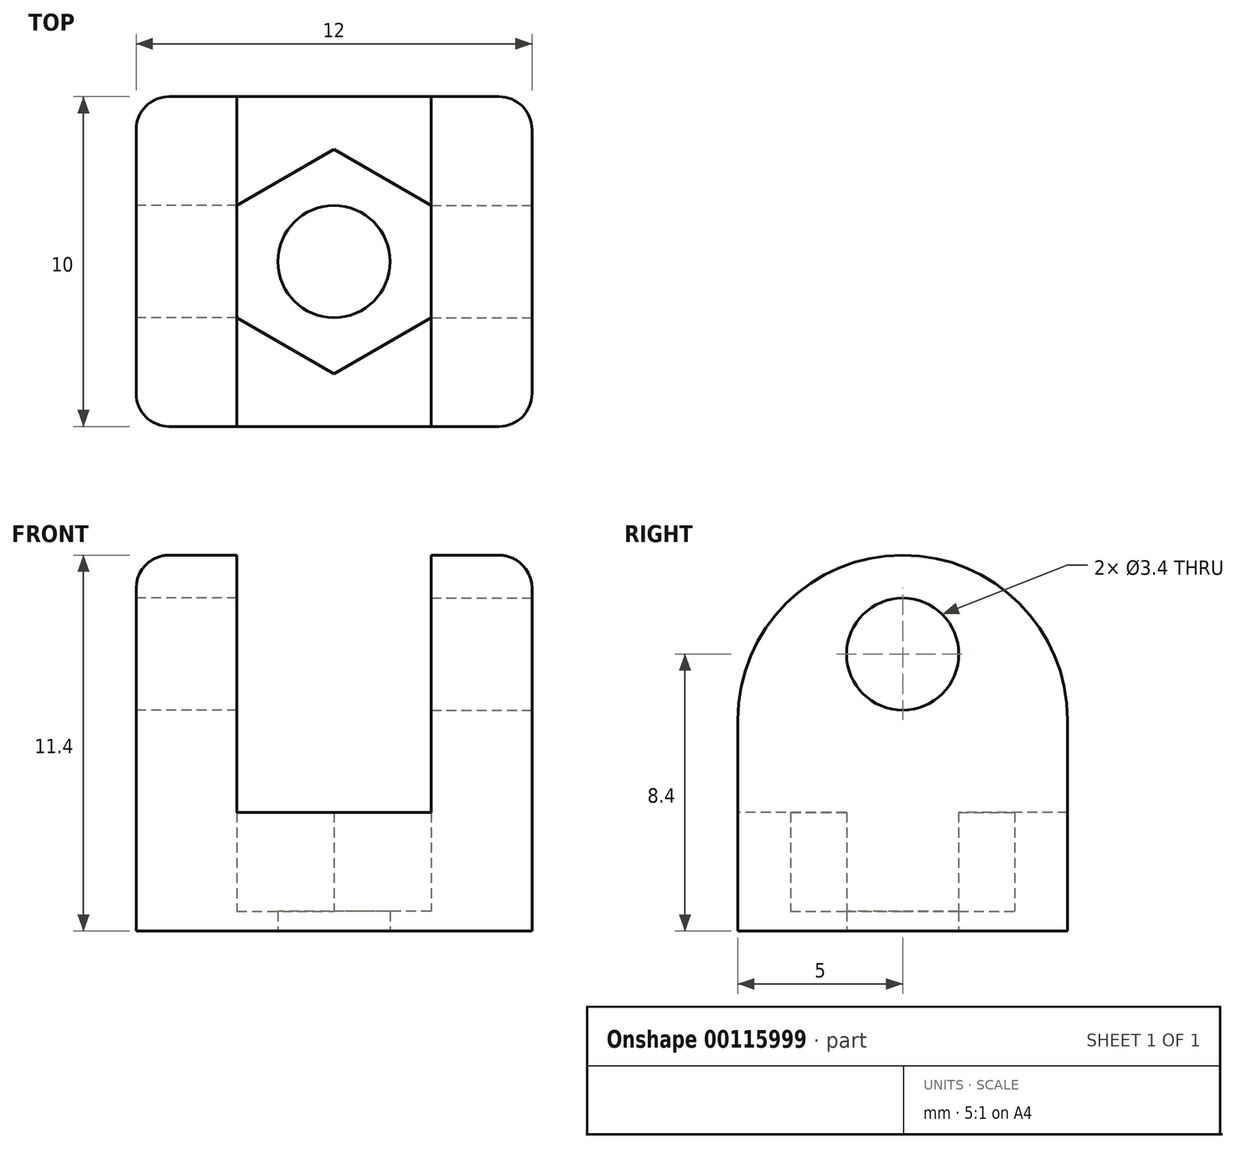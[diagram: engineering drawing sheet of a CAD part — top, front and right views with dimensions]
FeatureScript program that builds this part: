
annotation { "Feature Type Name" : "Feature", "Feature Type Description" : "" }
export const myFeature = defineFeature(function(context is Context, id is Id, definition is map)
    precondition{}
    {
        {
            var Q0;
            Q0=qCreatedBy(makeId("Top.planeOp"),FACE);
            var sketch = newSketch(context, id + "F0", { "sketchPlane" : qUnion([Q0])});
            skLineSegment(sketch, "E0.bottom", {"start": v(-6, 5) * mm, "end": v(6, 5) * mm});
            skLineSegment(sketch, "E0.top", {"start": v(-6, -5) * mm, "end": v(6, -5) * mm});
            skLineSegment(sketch, "E0.left", {"start": v(-6, 5) * mm, "end": v(-6, -5) * mm});
            skLineSegment(sketch, "E0.right", {"start": v(6, 5) * mm, "end": v(6, -5) * mm});
            skLineSegment(sketch, "E1", {"start": v(-2.94, 5) * mm, "end": v(-2.94, -5) * mm});
            skLineSegment(sketch, "E2", {"start": v(2.94, 5) * mm, "end": v(2.94, -5) * mm});
            skCircle(sketch, "E3", {"center": v(0, 0) * mm, "radius": 1.7 * mm});
            skCircle(sketch, "E4.cCircle", {"center": v(0, 0) * mm, "radius": 3.4 * mm, "construction": true});
            skLineSegment(sketch, "E4.0", {"start": v(0, 3.4) * mm, "end": v(2.94, 1.7) * mm});
            skLineSegment(sketch, "E4.1", {"start": v(2.94, 1.7) * mm, "end": v(2.94, -1.7) * mm});
            skLineSegment(sketch, "E4.2", {"start": v(2.94, -1.7) * mm, "end": v(0, -3.4) * mm});
            skLineSegment(sketch, "E4.3", {"start": v(0, -3.4) * mm, "end": v(-2.94, -1.7) * mm});
            skLineSegment(sketch, "E4.4", {"start": v(-2.94, -1.7) * mm, "end": v(-2.94, 1.7) * mm});
            skLineSegment(sketch, "E4.5", {"start": v(-2.94, 1.7) * mm, "end": v(0, 3.4) * mm});
            skSolve(sketch);
        }
        {
            var Q0;
            Q0=qCreatedBy(makeId("Right.planeOp"),FACE);
            cPlane(context, id + "F1", {"entities" : qUnion([Q0]), "cplaneType" : CPlaneType.OFFSET, "offset" : 7 * mm, "width" : 150 * mm, "height" : 150 * mm});
        }
        {
            var Q0;
            Q0=qCreatedBy(id+"F1.planeOp",FACE);
            var sketch = newSketch(context, id + "F2", { "sketchPlane" : qUnion([Q0])});
            skCircle(sketch, "E5", {"center": v(0, 8.4) * mm, "radius": 1.7 * mm});
            skSolve(sketch);
        }
        {
            var Q0;
            Q0=qCreatedBy(makeId("Right.planeOp"),FACE);
            cPlane(context, id + "F3", {"entities" : qUnion([Q0]), "cplaneType" : CPlaneType.OFFSET, "offset" : 7 * mm, "oppositeDirection" : true, "width" : 150 * mm, "height" : 150 * mm});
        }
        {
            var Q0;
            Q0=qCreatedBy(id+"F3.planeOp",FACE);
            var sketch = newSketch(context, id + "F4", { "sketchPlane" : qUnion([Q0])});
            skCircle(sketch, "E6", {"center": v(0, 8.4) * mm, "radius": 1.7 * mm});
            skSolve(sketch);
        }
        {
            var Q0;
            Q0=makeQuery(id+"F0.imprint","IMPRINT",FACE,{"disambiguationData":[TD([[makeQuery(id+"F0.imprint","IMPRINT",EDGE,{"derivedFrom":sQuery(id+"F0.wireOp",EDGE,"E3")}),-1.0]])]});
            extrude(context, id + "F5", {"entities" : qUnion([Q0]), "depth" : .6 * mm});
        }
        {
            var Q0;
            {var subQ1=sQuery(id+"F0.wireOp",EDGE,"E1");Q0=makeQuery(id+"F0.imprint","IMPRINT",FACE,{"disambiguationData":[TD([[makeQuery(id+"F0.imprint","IMPRINT",EDGE,{"derivedFrom":subQ1}),1.0]])]});}
            extrude(context, id + "F6", {"entities" : qUnion([Q0]), "operationType" : NewBodyOperationType.ADD, "depth" : 3.6 * mm});
        }
        {
            var Q0;
            {var subQ0=sQuery(id+"F0.wireOp",EDGE,"E0.left");Q0=makeQuery(id+"F0.imprint","IMPRINT",FACE,{"disambiguationData":[TD([[makeQuery(id+"F0.imprint","IMPRINT",EDGE,{"derivedFrom":subQ0}),1.0]])]});}
            var Q1;
            {var subQ0=sQuery(id+"F0.wireOp",EDGE,"E0.right");Q1=makeQuery(id+"F0.imprint","IMPRINT",FACE,{"disambiguationData":[TD([[makeQuery(id+"F0.imprint","IMPRINT",EDGE,{"derivedFrom":subQ0}),-1.0]])]});}
            extrude(context, id + "F7", {"entities" : qUnion([Q0, Q1]), "operationType" : NewBodyOperationType.ADD, "depth" : 11.4 * mm});
        }
        {
            var Q0;
            Q0=sQuery(id+"F4.wireOp",VERTEX,"E6.center");
            var Q1;
            Q1=makeQuery(id+"F5.opExtrude","SWEPT_BODY",BODY,{"disambiguationData":[OSD([sQuery(id+"F0.wireOp",EDGE,"E3"),sQuery(id+"F0.wireOp",EDGE,"E4.0"),sQuery(id+"F0.wireOp",EDGE,"E4.1"),sQuery(id+"F0.wireOp",EDGE,"E4.2"),sQuery(id+"F0.wireOp",EDGE,"E4.3"),sQuery(id+"F0.wireOp",EDGE,"E4.4"),sQuery(id+"F0.wireOp",EDGE,"E4.5")])]});
            hole(context, id + "F8", {"style" : HoleStyle.SIMPLE, "endStyle" : HoleEndStyle.BLIND, "oppositeDirection" : true, "holeDiameter" : 3.4 * mm, "holeDepth" : 5 * mm, "locations" : qUnion([Q0]), "scope" : qUnion([Q1])});
        }
        {
            var Q0;
            Q0=sQuery(id+"F2.wireOp",VERTEX,"E5.center");
            var Q1;
            Q1=makeQuery(id+"F5.opExtrude","SWEPT_BODY",BODY,{"disambiguationData":[OSD([sQuery(id+"F0.wireOp",EDGE,"E3"),sQuery(id+"F0.wireOp",EDGE,"E4.0"),sQuery(id+"F0.wireOp",EDGE,"E4.1"),sQuery(id+"F0.wireOp",EDGE,"E4.2"),sQuery(id+"F0.wireOp",EDGE,"E4.3"),sQuery(id+"F0.wireOp",EDGE,"E4.4"),sQuery(id+"F0.wireOp",EDGE,"E4.5")])]});
            hole(context, id + "F9", {"style" : HoleStyle.SIMPLE, "endStyle" : HoleEndStyle.BLIND, "holeDiameter" : 3.4 * mm, "holeDepth" : 5 * mm, "locations" : qUnion([Q0]), "scope" : qUnion([Q1])});
        }
        {
            var Q0;
            {var subQ0=sQuery(id+"F0.wireOp",EDGE,"E0.top");Q0=makeQuery(id+"F7.opExtrude","CAP_EDGE",EDGE,{"disambiguationData":[OSD([subQ0]),TDD([makeQuery(id+"F0.imprint","IMPRINT",EDGE,{"disambiguationData":[TD([[makeQuery(id+"F0.imprint","INTERSECT",VERTEX,{"derivedFrom":[subQ0,sQuery(id+"F0.wireOp",EDGE,"E0.left")]}),-1.0]])],"derivedFrom":subQ0})])],"isStart":false});}
            var Q1;
            {var subQ0=sQuery(id+"F0.wireOp",EDGE,"E0.bottom");Q1=makeQuery(id+"F7.opExtrude","CAP_EDGE",EDGE,{"disambiguationData":[OSD([subQ0]),TDD([makeQuery(id+"F0.imprint","IMPRINT",EDGE,{"disambiguationData":[TD([[makeQuery(id+"F0.imprint","INTERSECT",VERTEX,{"derivedFrom":[subQ0,sQuery(id+"F0.wireOp",EDGE,"E0.left")]}),-1.0]])],"derivedFrom":subQ0})])],"isStart":false});}
            var Q2;
            {var subQ0=sQuery(id+"F0.wireOp",EDGE,"E0.bottom");Q2=makeQuery(id+"F7.opExtrude","CAP_EDGE",EDGE,{"disambiguationData":[OSD([subQ0]),TDD([makeQuery(id+"F0.imprint","IMPRINT",EDGE,{"disambiguationData":[TD([[makeQuery(id+"F0.imprint","INTERSECT",VERTEX,{"derivedFrom":[subQ0,sQuery(id+"F0.wireOp",EDGE,"E0.right")]}),1.0]])],"derivedFrom":subQ0})])],"isStart":false});}
            var Q3;
            {var subQ0=sQuery(id+"F0.wireOp",EDGE,"E0.top");Q3=makeQuery(id+"F7.opExtrude","CAP_EDGE",EDGE,{"disambiguationData":[OSD([subQ0]),TDD([makeQuery(id+"F0.imprint","IMPRINT",EDGE,{"disambiguationData":[TD([[makeQuery(id+"F0.imprint","INTERSECT",VERTEX,{"derivedFrom":[subQ0,sQuery(id+"F0.wireOp",EDGE,"E0.right")]}),1.0]])],"derivedFrom":subQ0})])],"isStart":false});}
            fillet(context, id + "F10", {"entities" : qUnion([Q0, Q1, Q2, Q3]), "radius" : 5 * mm, "tangentPropagation" : true, "allowEdgeOverflow" : false});
        }
        {
            var Q0;
            {var subQ0=sQuery(id+"F0.wireOp",EDGE,"E0.right");var subQ1=sQuery(id+"F0.wireOp",EDGE,"E0.bottom");Q0=makeQuery(id+"F10.opFillet","BLEND_EDGE",EDGE,{"blendedFrom":[makeQuery(id+"F7.opExtrude","CAP_EDGE",EDGE,{"disambiguationData":[OSD([subQ1]),TDD([makeQuery(id+"F0.imprint","IMPRINT",EDGE,{"disambiguationData":[TD([[makeQuery(id+"F0.imprint","INTERSECT",VERTEX,{"derivedFrom":[subQ1,subQ0]}),1.0]])],"derivedFrom":subQ1})])],"isStart":false}),makeQuery(id+"F7.opExtrude","SWEPT_FACE",FACE,{"disambiguationData":[OSD([subQ0])]})],"blendedInto":[makeQuery(id+"F7.opExtrude","SWEPT_FACE",FACE,{"disambiguationData":[OSD([subQ0])]})]});}
            var Q1;
            {var subQ0=sQuery(id+"F0.wireOp",EDGE,"E0.left");var subQ1=sQuery(id+"F0.wireOp",EDGE,"E0.bottom");Q1=makeQuery(id+"F10.opFillet","BLEND_EDGE",EDGE,{"blendedFrom":[makeQuery(id+"F7.opExtrude","CAP_EDGE",EDGE,{"disambiguationData":[OSD([subQ1]),TDD([makeQuery(id+"F0.imprint","IMPRINT",EDGE,{"disambiguationData":[TD([[makeQuery(id+"F0.imprint","INTERSECT",VERTEX,{"derivedFrom":[subQ1,subQ0]}),-1.0]])],"derivedFrom":subQ1})])],"isStart":false}),makeQuery(id+"F7.opExtrude","SWEPT_FACE",FACE,{"disambiguationData":[OSD([subQ0])]})],"blendedInto":[makeQuery(id+"F7.opExtrude","SWEPT_FACE",FACE,{"disambiguationData":[OSD([subQ0])]})]});}
            fillet(context, id + "F11", {"entities" : qUnion([Q0, Q1]), "radius" : 1 * mm, "tangentPropagation" : true, "allowEdgeOverflow" : false});
        }
    });
